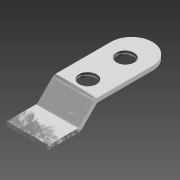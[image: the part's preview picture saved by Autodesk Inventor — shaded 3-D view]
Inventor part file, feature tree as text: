
AUTODESK INVENTOR PART (.ipt)
format: ipt  version: 2015 (Build 190159000, 159)  size: 141,824 bytes
history: native  units: mm
features: sketch x3, sweep x1, fillet x1, hole x1, pattern_linear x1, other x1
ambient origin geometry x8: Origin, YZ Plane, XZ Plane, XY Plane, X Axis, Y Axis, Z Axis, Center Point
bodies: Body1 (feature_tree)
feature tree (8):
  sweep  "Przeciągnięcie1"
  fillet  "Zaokrąglenie1"  Radius=20.594885mm
  hole  "Otwór1"  [1 undecoded]
  pattern_linear  "Szyk prostokątny2"  Spacing1=2.0mm  [1 undecoded]
  sketch  "Szkic1"
  sketch  "Szkic2"
  sketch  "Szkic5"
  other  "Bryła3"
note: 2 required parameter values undecoded (feature->parameter linkage not recoverable at this tier; creation-order binding heuristic only, values carry confidence <= 0.55)
